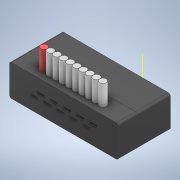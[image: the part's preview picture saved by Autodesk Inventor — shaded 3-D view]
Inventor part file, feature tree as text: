
AUTODESK INVENTOR PART (.ipt)
format: ipt  version: 2020 (Build 240168000, 168)  size: 255,488 bytes
history: native  units: mm
features: imported_body x9, other x5, fillet x1, sketch x1
ambient origin geometry x8: Origin, YZ Plane, XZ Plane, XY Plane, X Axis, Y Axis, Z Axis, Center Point
bodies: Solid1 (feature_tree), Solid2 (feature_tree), Solid3 (feature_tree), Solid4 (feature_tree), Solid5 (feature_tree), Solid6 (feature_tree), Solid7 (feature_tree), Solid8 (feature_tree), Solid9 (feature_tree), Solid10 (feature_tree), Solid11 (feature_tree), Solid12 (feature_tree), Solid13 (feature_tree), Solid14 (feature_tree)
feature tree (16):
  fillet  "Fillet1"  Radius=0.2mm
  sketch  "Sketch1"
  other  "Твердое тело5"
  imported_body  "Imported2"
  other  "Твердое тело1"
  other  "Твердое тело2"
  other  "Твердое тело3"
  imported_body  "Imported6"
  other  "Твердое тело4"
  imported_body  "Imported8"
  imported_body  "Imported9"
  imported_body  "Imported10"
  imported_body  "Imported11"
  imported_body  "Imported12"
  imported_body  "Imported13"
  imported_body  "Imported14"
